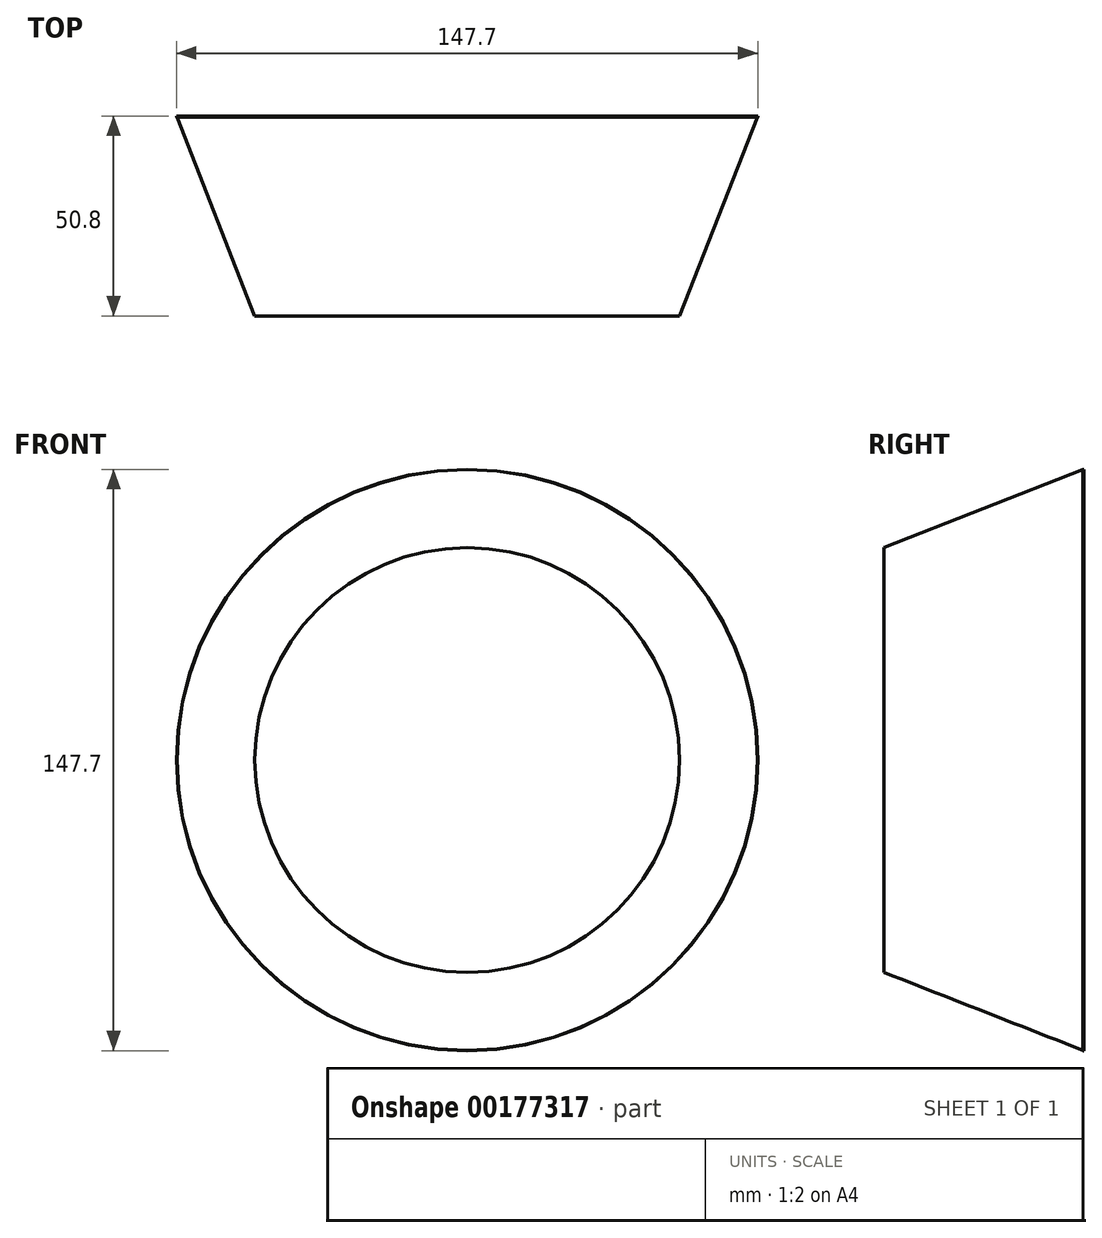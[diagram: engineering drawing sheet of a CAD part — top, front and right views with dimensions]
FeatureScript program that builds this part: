
annotation { "Feature Type Name" : "Feature", "Feature Type Description" : "" }
export const myFeature = defineFeature(function(context is Context, id is Id, definition is map)
    precondition{}
    {
        {
            var Q0;
            Q0=qCreatedBy(makeId("Front.planeOp"),FACE);
            var sketch = newSketch(context, id + "F0", { "sketchPlane" : qUnion([Q0])});
            skCircle(sketch, "E0", {"center": v(0, 0) * mm, "radius": 73.85 * mm});
            skSolve(sketch);
        }
        {
            var Q0;
            Q0=makeQuery(id+"F0.imprint","IMPRINT",FACE,{"disambiguationData":[TD([[makeQuery(id+"F0.imprint","IMPRINT",EDGE,{"derivedFrom":sQuery(id+"F0.wireOp",EDGE,"E0")}),1.0]])]});
            extrude(context, id + "F1", {"entities" : qUnion([Q0]), "depth" : 50.8 * mm});
        }
        {
            var Q0;
            Q0=makeQuery(id+"F1.opExtrude","CAP_FACE",FACE,{"disambiguationData":[OSD([sQuery(id+"F0.wireOp",EDGE,"E0")])],"isStart":false});
            var sketch = newSketch(context, id + "F2", { "sketchPlane" : qUnion([Q0])});
            skCircle(sketch, "E1", {"center": v(0, 0) * mm, "radius": 53.95 * mm});
            skSolve(sketch);
        }
        {
            var Q0;
            Q0=makeQuery(id+"F2.imprint","IMPRINT",FACE,{"disambiguationData":[TD([[makeQuery(id+"F2.imprint","IMPRINT",EDGE,{"derivedFrom":sQuery(id+"F2.wireOp",EDGE,"E1")}),-1.0]])]});
            extrude(context, id + "F3", {"entities" : qUnion([Q0]), "operationType" : NewBodyOperationType.REMOVE, "oppositeDirection" : true, "depth" : 50.55 * mm});
        }
        {
            var Q1;
            Q1=makeQuery(id+"F1.opExtrude","CAP_FACE",FACE,{"disambiguationData":[OSD([sQuery(id+"F0.wireOp",EDGE,"E0")])],"isStart":true});
            var Q2;
            Q2=makeQuery(id+"F1.opExtrude","CAP_FACE",FACE,{"disambiguationData":[OSD([sQuery(id+"F0.wireOp",EDGE,"E0")])],"isStart":false});
            loft(context, id + "F4", {"operationType" : NewBodyOperationType.ADD, "sheetProfilesArray" : [{ "sheetProfileEntities" : qUnion([Q1]) }, { "sheetProfileEntities" : qUnion([Q2]) }]});
        }
    });
